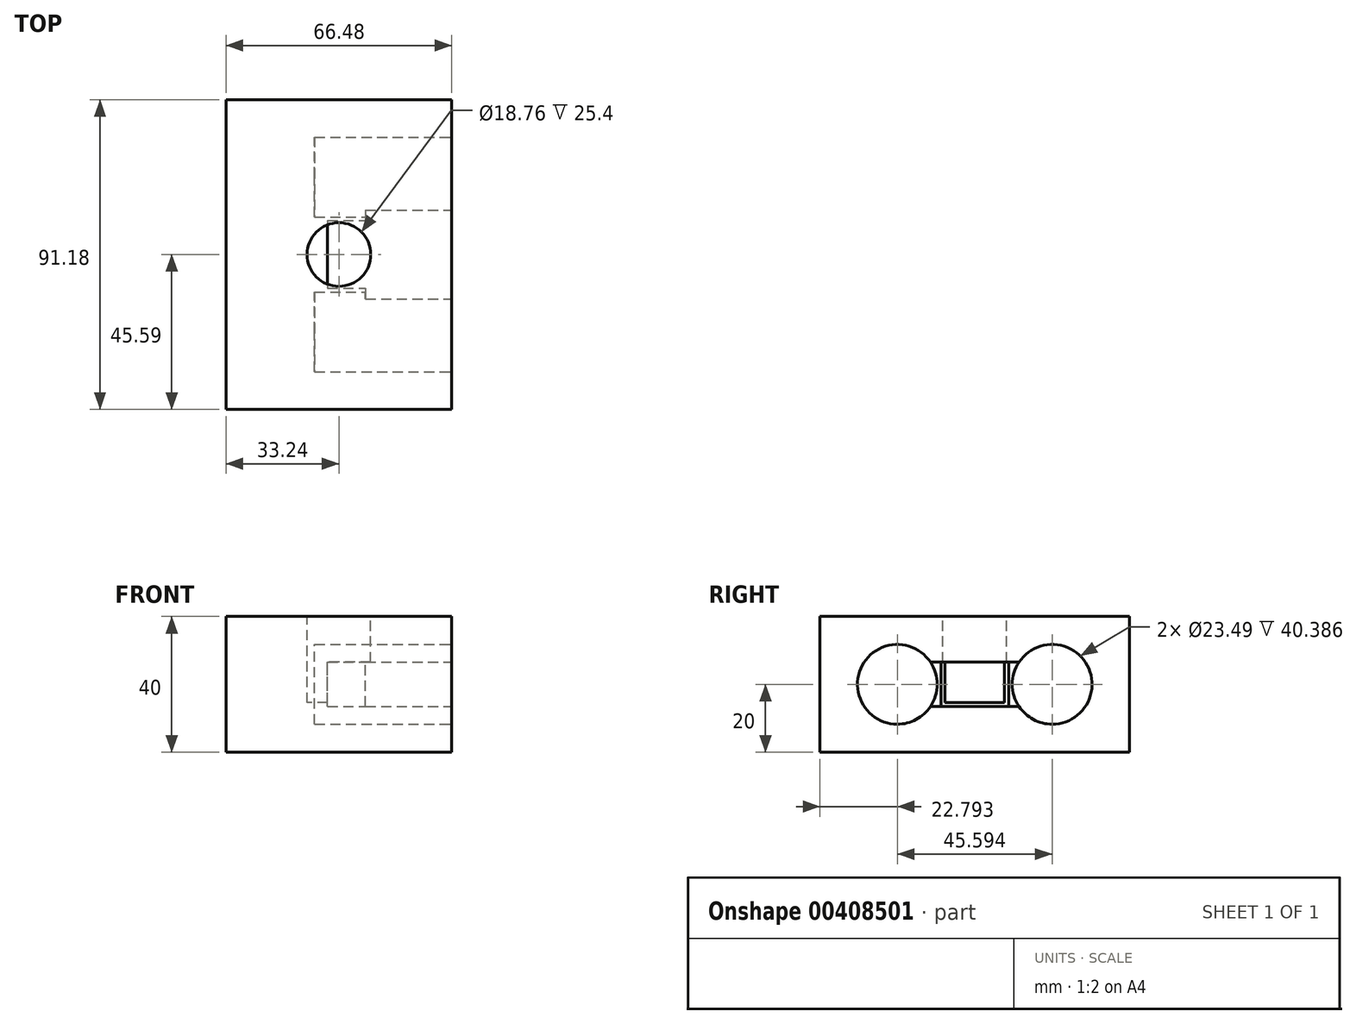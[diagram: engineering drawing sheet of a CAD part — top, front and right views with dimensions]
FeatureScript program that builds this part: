
annotation { "Feature Type Name" : "Feature", "Feature Type Description" : "" }
export const myFeature = defineFeature(function(context is Context, id is Id, definition is map)
    precondition{}
    {
        {
            var Q0;
            Q0=qCreatedBy(makeId("Top.planeOp"),FACE);
            var sketch = newSketch(context, id + "F0", { "sketchPlane" : qUnion([Q0])});
            skLineSegment(sketch, "E0.bottom", {"start": v(33.24, -45.6) * mm, "end": v(-33.24, -45.6) * mm});
            skLineSegment(sketch, "E0.top", {"start": v(33.24, 45.6) * mm, "end": v(-33.24, 45.6) * mm});
            skLineSegment(sketch, "E0.left", {"start": v(33.24, -45.6) * mm, "end": v(33.24, 45.6) * mm});
            skLineSegment(sketch, "E0.right", {"start": v(-33.24, -45.6) * mm, "end": v(-33.24, 45.6) * mm});
            skPoint(sketch, "E0.middle", {"position": v(0, 0) * mm});
            skSolve(sketch);
        }
        {
            var Q0;
            Q0=makeQuery(id+"F0.imprint","IMPRINT",FACE,{"disambiguationData":[TD([[makeQuery(id+"F0.imprint","IMPRINT",EDGE,{"derivedFrom":sQuery(id+"F0.wireOp",EDGE,"E0.bottom")}),-1.0]])]});
            extrude(context, id + "F1", {"entities" : qUnion([Q0]), "depth" : 40 * mm});
        }
        {
            var Q0;
            Q0=makeQuery(id+"F1.opExtrude","SWEPT_FACE",FACE,{"disambiguationData":[OSD([sQuery(id+"F0.wireOp",EDGE,"E0.left")])]});
            var sketch = newSketch(context, id + "F2", { "sketchPlane" : qUnion([Q0])});
            skCircle(sketch, "E1", {"center": v(-22.8, 20) * mm, "radius": 11.75 * mm});
            skCircle(sketch, "E2", {"center": v(22.8, 20) * mm, "radius": 11.75 * mm});
            skSolve(sketch);
        }
        {
            var Q0;
            Q0 = qSketchRegion(id + "F2", true);
            extrude(context, id + "F3", {"entities" : qUnion([Q0]), "operationType" : NewBodyOperationType.REMOVE, "oppositeDirection" : true, "depth" : 40.4 * mm});
        }
        {
            var Q0;
            Q0=makeQuery(id+"F1.opExtrude","CAP_FACE",FACE,{"disambiguationData":[OSD([sQuery(id+"F0.wireOp",EDGE,"E0.bottom"),sQuery(id+"F0.wireOp",EDGE,"E0.top"),sQuery(id+"F0.wireOp",EDGE,"E0.left"),sQuery(id+"F0.wireOp",EDGE,"E0.right")])],"isStart":false});
            var sketch = newSketch(context, id + "F4", { "sketchPlane" : qUnion([Q0])});
            skCircle(sketch, "E3", {"center": v(0, 0) * mm, "radius": 9.38 * mm});
            skSolve(sketch);
        }
        {
            var Q0;
            Q0 = qSketchRegion(id + "F4", true);
            extrude(context, id + "F5", {"entities" : qUnion([Q0]), "operationType" : NewBodyOperationType.REMOVE, "oppositeDirection" : true, "depth" : 25.4 * mm});
        }
        {
            var Q0;
            Q0=makeQuery(id+"F1.opExtrude","SWEPT_FACE",FACE,{"disambiguationData":[OSD([sQuery(id+"F0.wireOp",EDGE,"E0.left")])]});
            var sketch = newSketch(context, id + "F6", { "sketchPlane" : qUnion([Q0])});
            skLineSegment(sketch, "E4.bottom", {"start": v(13.03, 13.47) * mm, "end": v(-13.03, 13.47) * mm});
            skLineSegment(sketch, "E4.top", {"start": v(13.03, 26.53) * mm, "end": v(-13.03, 26.53) * mm});
            skLineSegment(sketch, "E4.left", {"start": v(13.03, 13.47) * mm, "end": v(13.03, 26.53) * mm});
            skLineSegment(sketch, "E4.right", {"start": v(-13.03, 13.47) * mm, "end": v(-13.03, 26.53) * mm});
            skPoint(sketch, "E4.middle", {"position": v(0, 20) * mm});
            skPoint(sketch, "E4.middle.positionSnap0", {"position": v(-45.6, 20) * mm});
            skPoint(sketch, "E4.centerSnap0", {"position": v(-45.6, 20) * mm});
            skSolve(sketch);
        }
        {
            var Q0;
            Q0 = qSketchRegion(id + "F6", true);
            extrude(context, id + "F7", {"entities" : qUnion([Q0]), "operationType" : NewBodyOperationType.REMOVE, "oppositeDirection" : true, "depth" : 25.4 * mm});
        }
        {
            var Q0;
            Q0=makeQuery(id+"F1.opExtrude","SWEPT_FACE",FACE,{"disambiguationData":[OSD([sQuery(id+"F0.wireOp",EDGE,"E0.left")])]});
            var sketch = newSketch(context, id + "F8", { "sketchPlane" : qUnion([Q0])});
            skLineSegment(sketch, "E5", {"start": v(-13.03, 26.53) * mm, "end": v(13.03, 13.47) * mm});
            skLineSegment(sketch, "E6", {"start": v(13.03, 26.53) * mm, "end": v(-13.03, 13.47) * mm});
            skLineSegment(sketch, "E7.bottom", {"start": v(9.97, 13.47) * mm, "end": v(-9.97, 13.47) * mm});
            skLineSegment(sketch, "E7.top", {"start": v(9.97, 26.53) * mm, "end": v(-9.97, 26.53) * mm});
            skLineSegment(sketch, "E7.left", {"start": v(9.97, 13.47) * mm, "end": v(9.97, 26.53) * mm});
            skLineSegment(sketch, "E7.right", {"start": v(-9.97, 13.47) * mm, "end": v(-9.97, 26.53) * mm});
            skPoint(sketch, "E7.middle", {"position": v(0, 20) * mm});
            skSolve(sketch);
        }
        {
            var Q0;
            Q0 = qSketchRegion(id + "F8", true);
            extrude(context, id + "F9", {"entities" : qUnion([Q0]), "operationType" : NewBodyOperationType.REMOVE, "oppositeDirection" : true, "depth" : 36.58 * mm});
        }
    });
